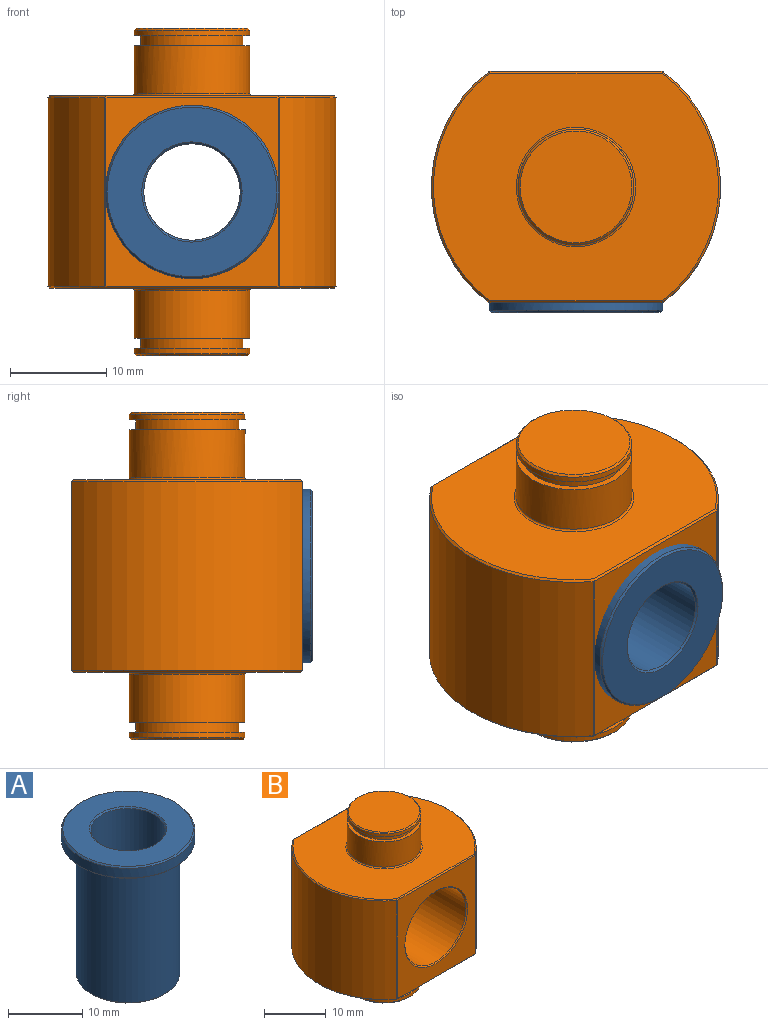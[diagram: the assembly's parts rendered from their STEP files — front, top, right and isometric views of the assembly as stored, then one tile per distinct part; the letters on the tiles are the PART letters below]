
ASSEMBLY  parts=2 mates=1
PART A: 12 faces, bbox 18x18x24 mm
  f0: plane 17.6x17.6mm, normal (0,0,1), area 158.3mm2, adj f6,f7
  f1: cylinder r=9mm len=18mm, axis (0,0,1), area 90.5mm2, adj f7,f8
  f2: plane 17.6x17.6mm, normal (0,0,-1), area 80.9mm2, adj f8,f11
  f3: cylinder r=6.99mm len=21.6mm, axis (0,0,1), area 948.7mm2, adj f9,f11
  f4: plane 13.58x13.58mm, normal (0,0,-1), area 59.9mm2, adj f9,f10
  f5: cylinder r=5mm len=23.6mm, axis (0,0,1), area 741.4mm2, adj f6,f10
  f6: cone r=5mm half-angle=45deg, axis (0,0,1), area 9.1mm2, adj f0,f5
  f7: cone r=8.8mm half-angle=45deg, axis (0,0,-1), area 15.8mm2, adj f0,f1
  f8: cone r=9mm half-angle=45deg, axis (0,0,1), area 15.8mm2, adj f1,f2
  f9: cone r=6.99mm half-angle=45deg, axis (0,0,1), area 12.2mm2, adj f3,f4
  f10: cone r=5mm half-angle=45deg, axis (0,0,-1), area 9.1mm2, adj f4,f5
  f11: torus R=7.19mm, axis (0,0,-1), area 13.9mm2, adj f2,f3
PART B: 45 faces, bbox 30x24x34 mm
  f0: cylinder r=6mm len=12mm, axis (0,0,1), area 188.5mm2, adj f32,f35
  f1: cylinder r=15mm len=23.92mm, axis (0,0,1), area 542.6mm2, adj f5,f8,f13,f14,f16,f21,f22,f24
  f2: cylinder r=15mm len=23.92mm, axis (0,0,1), area 542.6mm2, adj f6,f7,f17,f19,f20,f25,f27,f28
  f3: plane 29.6x23.6mm, normal (0,0,1), area 494.3mm2, adj f7,f8,f15,f23,f31
  f4: plane 29.6x23.6mm, normal (0,0,-1), area 494.3mm2, adj f5,f6,f18,f26,f32
  f5: cone r=15mm half-angle=45deg, axis (0,0,1), area 7.8mm2, adj f1,f4,f16,f18,f24,f26
  f6: cone r=15mm half-angle=45deg, axis (0,0,1), area 7.8mm2, adj f2,f4,f18,f20,f26,f28
  f7: cone r=14.8mm half-angle=45deg, axis (0,0,-1), area 7.8mm2, adj f2,f3,f15,f17,f23,f25
  f8: cone r=14.8mm half-angle=45deg, axis (0,0,-1), area 7.8mm2, adj f1,f3,f13,f15,f21,f23
  f9: cylinder r=6mm len=12mm, axis (0,0,1), area 188.5mm2, adj f31,f40
  f10: plane 19.6x17.87mm, normal (0,-1,0), area 187.3mm2, adj f21,f22,f23,f24,f25,f26,f27,f28
  f11: plane 19.6x17.87mm, normal (0,1,0), area 187.3mm2, adj f13,f14,f15,f16,f17,f18,f19,f20
  f12: cylinder r=7mm len=23.6mm, axis (0,1,0), area 1038mm2, adj f29,f30
  f13: bspline ~0.55x0.42mm, area 0mm2, adj f1,f8,f11,f14,f15
  f14: plane 19.48x0.13mm, normal (0.32,0.95,0), area 2.5mm2, adj f1,f11,f13,f16
  f15: plane 17.94x0.2mm, normal (0,0.71,0.71), area 5mm2, adj f3,f7,f8,f11,f13,f17
  f16: bspline ~0.55x0.42mm, area 0mm2, adj f1,f5,f11,f14,f18
  f17: bspline ~0.55x0.42mm, area 0mm2, adj f2,f7,f11,f15,f19
  f18: plane 17.94x0.2mm, normal (0,0.71,-0.71), area 5mm2, adj f4,f5,f6,f11,f16,f20
  f19: plane 19.47x0.13mm, normal (-0.32,0.95,0), area 2.5mm2, adj f2,f11,f17,f20
  f20: bspline ~0.32x0.28mm, area 0mm2, adj f2,f6,f11,f18,f19
  f21: bspline ~0.55x0.42mm, area 0mm2, adj f1,f8,f10,f22,f23
  f22: plane 19.48x0.13mm, normal (0.32,-0.95,0), area 2.5mm2, adj f1,f10,f21,f24
  f23: plane 17.94x0.2mm, normal (0,-0.71,0.71), area 5mm2, adj f3,f7,f8,f10,f21,f25
  f24: bspline ~0.32x0.28mm, area 0mm2, adj f1,f5,f10,f22,f26
  f25: bspline ~0.55x0.42mm, area 0mm2, adj f2,f7,f10,f23,f27
  f26: plane 17.94x0.2mm, normal (0,-0.71,-0.71), area 5mm2, adj f4,f5,f6,f10,f24,f28
  f27: plane 19.47x0.13mm, normal (-0.32,-0.95,0), area 2.5mm2, adj f2,f10,f25,f28
  f28: bspline ~0.55x0.42mm, area 0mm2, adj f2,f6,f10,f26,f27
  f29: cone r=7mm half-angle=45deg, axis (0,-1,0), area 12.6mm2, adj f10,f12
  f30: cone r=7.2mm half-angle=45deg, axis (0,1,0), area 12.6mm2, adj f11,f12
  f31: torus R=6.2mm, axis (0,0,1), area 12mm2, adj f3,f9
  f32: torus R=6.2mm, axis (0,0,-1), area 12mm2, adj f0,f4
  f33: plane 12x12mm, normal (0,0,1), area 23.2mm2, adj f34,f38
  f34: cylinder r=5.35mm len=10.7mm, axis (0,0,-1), area 33.6mm2, adj f33,f35
  f35: plane 12x12mm, normal (0,0,-1), area 23.2mm2, adj f0,f34
  f36: plane 11.6x11.6mm, normal (0,0,-1), area 105.7mm2, adj f37
  f37: cone r=6mm half-angle=45deg, axis (0,0,1), area 10.5mm2, adj f36,f38
  f38: cylinder r=6mm len=12mm, axis (0,0,1), area 22.6mm2, adj f33,f37
  f39: plane 12x12mm, normal (0,0,-1), area 23.2mm2, adj f41,f44
  f40: plane 12x12mm, normal (0,0,1), area 23.2mm2, adj f9,f41
  f41: cylinder r=5.35mm len=10.7mm, axis (0,0,-1), area 33.6mm2, adj f39,f40
  f42: plane 11.6x11.6mm, normal (0,0,1), area 105.7mm2, adj f43
  f43: cone r=5.8mm half-angle=45deg, axis (0,0,-1), area 10.5mm2, adj f42,f44
  f44: cylinder r=6mm len=12mm, axis (0,0,1), area 22.6mm2, adj f39,f43
PLACE A rot(axis=(1,0,0),90deg) t=(6.83,-0.59,2.2)mm
PLACE B t=(6.83,0.41,2.2)mm
MATE fastened A.f1 <-> B.f12  axis (0,-1,0) through (6.83,0.41,2.2)mm
